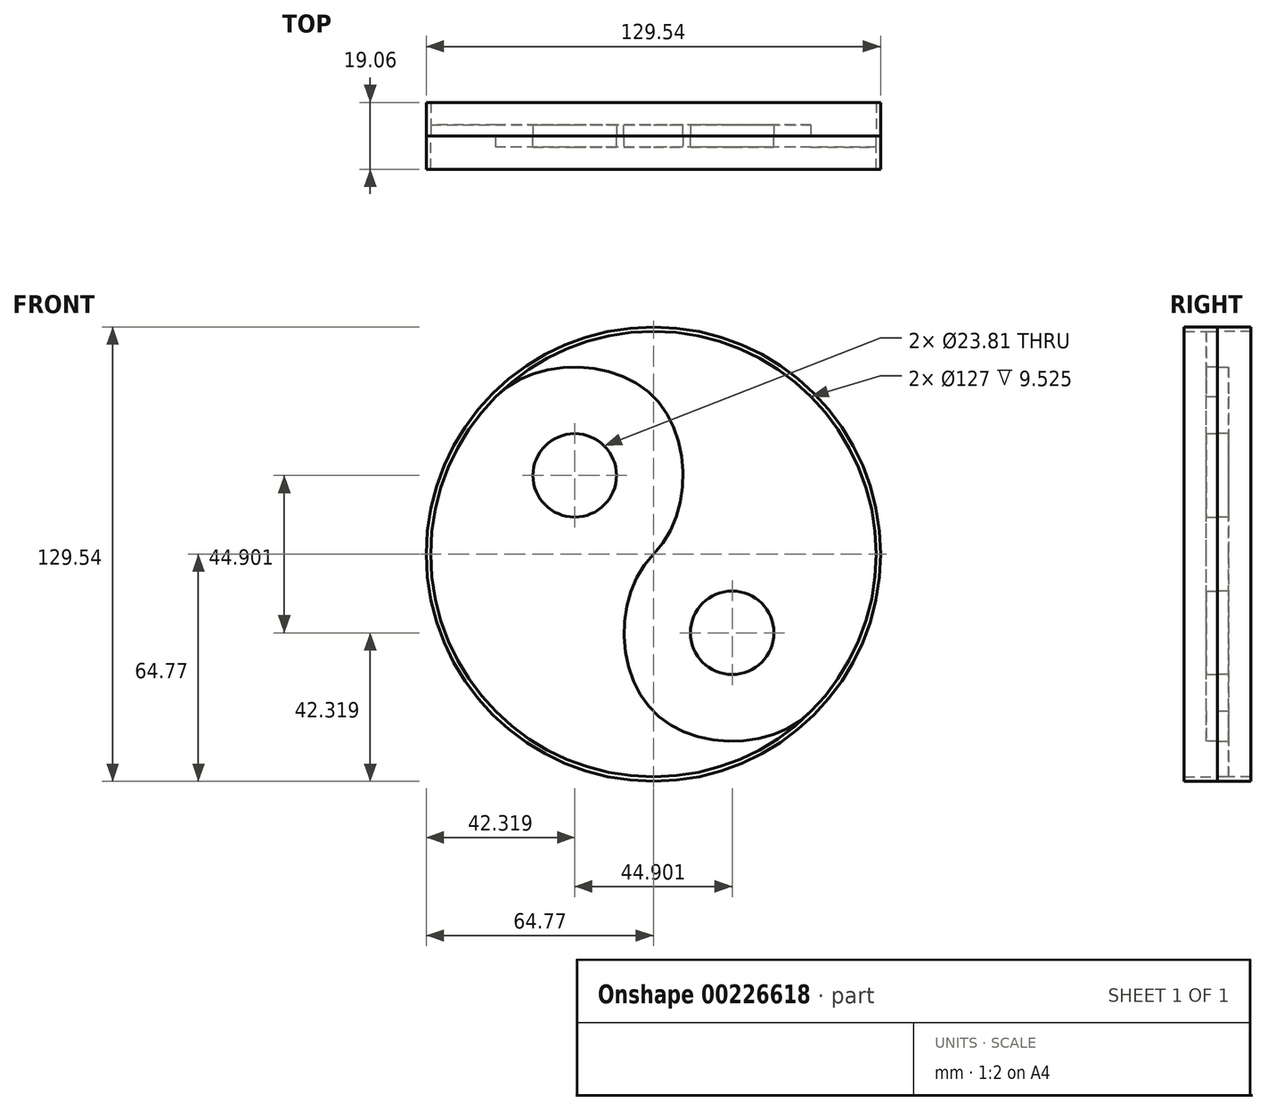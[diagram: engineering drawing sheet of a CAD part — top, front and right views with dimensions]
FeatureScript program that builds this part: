
annotation { "Feature Type Name" : "Feature", "Feature Type Description" : "" }
export const myFeature = defineFeature(function(context is Context, id is Id, definition is map)
    precondition{}
    {
        {
            var Q0;
            Q0=qCreatedBy(makeId("Front.planeOp"),FACE);
            var sketch = newSketch(context, id + "F0", { "sketchPlane" : qUnion([Q0])});
            skCircle(sketch, "E0", {"center": v(0, 0) * mm, "radius": 63.5 * mm});
            skLineSegment(sketch, "E1", {"start": v(0, 0) * mm, "end": v(0, 63.5) * mm, "construction": true});
            skLineSegment(sketch, "E2", {"start": v(0, 63.5) * mm, "end": v(-63.5, 0) * mm, "construction": true});
            skLineSegment(sketch, "E3", {"start": v(0, -63.5) * mm, "end": v(63.5, 0) * mm, "construction": true});
            skLineSegment(sketch, "E4", {"start": v(63.5, 0) * mm, "end": v(0, 0) * mm, "construction": true});
            skLineSegment(sketch, "E5", {"start": v(-44.9, 0) * mm, "end": v(0, 44.9) * mm, "construction": true});
            skFitSpline(sketch, "E6", {"points": [v(-44.9, 44.9) * mm, v(-44.9, 0) * mm, v(0, 0) * mm, v(0, 44.9) * mm, v(-44.9, 44.9) * mm]});
            skLineSegment(sketch, "E7", {"start": v(0, -44.9) * mm, "end": v(44.9, 0) * mm, "construction": true});
            skFitSpline(sketch, "E8", {"points": [v(0, 0) * mm, v(44.9, 0) * mm, v(44.9, -44.9) * mm, v(0, -44.9) * mm, v(0, 0) * mm]});
            skLineSegment(sketch, "E9", {"start": v(-44.9, 0) * mm, "end": v(0, -63.5) * mm, "construction": true});
            skLineSegment(sketch, "E10", {"start": v(-44.9, 44.9) * mm, "end": v(-22.45, 22.45) * mm});
            skLineSegment(sketch, "E11", {"start": v(-22.45, 22.45) * mm, "end": v(0, 0) * mm});
            skLineSegment(sketch, "E12", {"start": v(0, 0) * mm, "end": v(22.45, -22.45) * mm, "construction": true});
            skLineSegment(sketch, "E13", {"start": v(22.45, -22.45) * mm, "end": v(44.9, -44.9) * mm, "construction": true});
            skLineSegment(sketch, "E14", {"start": v(0, -44.9) * mm, "end": v(44.9, -44.9) * mm, "construction": true});
            skCircle(sketch, "E15", {"center": v(-22.45, 22.45) * mm, "radius": 11.9 * mm});
            skCircle(sketch, "E16", {"center": v(22.45, -22.45) * mm, "radius": 11.9 * mm});
            skSolve(sketch);
        }
        {
            var Q0;
            {var subQ1=sQuery(id+"F0.wireOp",EDGE,"E0");var subQ3=sQuery(id+"F0.wireOp",EDGE,"E8");var subQ4=makeQuery(id+"F0.imprint","INTERSECT",VERTEX,{"derivedFrom":[subQ1,subQ3]});Q0=makeQuery(id+"F0.imprint","IMPRINT",FACE,{"disambiguationData":[TD([[makeQuery(id+"F0.imprint","IMPRINT",EDGE,{"disambiguationData":[TD([[subQ4,-1.0]])],"derivedFrom":subQ3}),1.0]])]});}
            var Q1;
            {var subQ4=sQuery(id+"F0.wireOp",EDGE,"E15");var subQ6=sQuery(id+"F0.wireOp",EDGE,"E10");var subQ8=makeQuery(id+"F0.imprint","INTERSECT",VERTEX,{"derivedFrom":[subQ6,subQ4]});Q1=makeQuery(id+"F0.imprint","IMPRINT",FACE,{"disambiguationData":[TD([[makeQuery(id+"F0.imprint","IMPRINT",EDGE,{"disambiguationData":[TD([[subQ8,-1.0]])],"derivedFrom":subQ4}),-1.0]])]});}
            var Q2;
            {var subQ0=sQuery(id+"F0.wireOp",EDGE,"E10");var subQ5=sQuery(id+"F0.wireOp",EDGE,"E15");var subQ6=makeQuery(id+"F0.imprint","INTERSECT",VERTEX,{"derivedFrom":[subQ0,subQ5]});Q2=makeQuery(id+"F0.imprint","IMPRINT",FACE,{"disambiguationData":[TD([[makeQuery(id+"F0.imprint","IMPRINT",EDGE,{"disambiguationData":[TD([[subQ6,1.0]])],"derivedFrom":subQ5}),-1.0]])]});}
            var Q3;
            Q3=makeQuery(id+"F0.imprint","IMPRINT",FACE,{"disambiguationData":[TD([[makeQuery(id+"F0.imprint","IMPRINT",EDGE,{"derivedFrom":sQuery(id+"F0.wireOp",EDGE,"E16")}),1.0]])]});
            extrude(context, id + "F1", {"entities" : qUnion([Q0, Q1, Q2, Q3]), "oppositeDirection" : true, "depth" : 3.17 * mm});
        }
        {
            var Q0;
            Q0=qCreatedBy(makeId("Front.planeOp"),FACE);
            var sketch = newSketch(context, id + "F2", { "sketchPlane" : qUnion([Q0])});
            skCircle(sketch, "E17", {"center": v(0, 0) * mm, "radius": 63.5 * mm});
            skCircle(sketch, "E18", {"center": v(0, 0) * mm, "radius": 64.77 * mm});
            skSolve(sketch);
        }
        {
            var Q0;
            Q0 = qSketchRegion(id + "F2", true);
            extrude(context, id + "F3", {"entities" : qUnion([Q0]), "operationType" : NewBodyOperationType.ADD, "depth" : 9.52 * mm});
        }
        {
            var Q0;
            {var subQ1=sQuery(id+"F0.wireOp",EDGE,"E0");var subQ3=sQuery(id+"F0.wireOp",EDGE,"E8");var subQ4=makeQuery(id+"F0.imprint","INTERSECT",VERTEX,{"derivedFrom":[subQ1,subQ3]});Q0=makeQuery(id+"F0.imprint","IMPRINT",FACE,{"disambiguationData":[TD([[makeQuery(id+"F0.imprint","IMPRINT",EDGE,{"disambiguationData":[TD([[subQ4,-1.0]])],"derivedFrom":subQ1}),1.0]])]});}
            var Q1;
            Q1=makeQuery(id+"F0.imprint","IMPRINT",FACE,{"disambiguationData":[TD([[makeQuery(id+"F0.imprint","IMPRINT",EDGE,{"derivedFrom":sQuery(id+"F0.wireOp",EDGE,"E16")}),-1.0]])]});
            var Q2;
            {var subQ0=sQuery(id+"F0.wireOp",EDGE,"E11");var subQ1=sQuery(id+"F0.wireOp",EDGE,"E10");var subQ2=makeQuery(id+"F0.imprint","INTERSECT",VERTEX,{"derivedFrom":[subQ1,subQ0]});Q2=makeQuery(id+"F0.imprint","IMPRINT",FACE,{"disambiguationData":[TD([[makeQuery(id+"F0.imprint","IMPRINT",EDGE,{"disambiguationData":[TD([[subQ2,1.0]])],"derivedFrom":subQ1}),-1.0]])]});}
            var Q3;
            {var subQ0=sQuery(id+"F0.wireOp",EDGE,"E11");var subQ1=sQuery(id+"F0.wireOp",EDGE,"E10");var subQ2=makeQuery(id+"F0.imprint","INTERSECT",VERTEX,{"derivedFrom":[subQ1,subQ0]});Q3=makeQuery(id+"F0.imprint","IMPRINT",FACE,{"disambiguationData":[TD([[makeQuery(id+"F0.imprint","IMPRINT",EDGE,{"disambiguationData":[TD([[subQ2,1.0]])],"derivedFrom":subQ1}),1.0]])]});}
            extrude(context, id + "F4", {"entities" : qUnion([Q0, Q1, Q2, Q3]), "depth" : 3.17 * mm});
        }
        {
            var Q0;
            Q0 = qSketchRegion(id + "F2", true);
            extrude(context, id + "F5", {"entities" : qUnion([Q0]), "oppositeDirection" : true, "depth" : 9.52 * mm});
        }
    });
